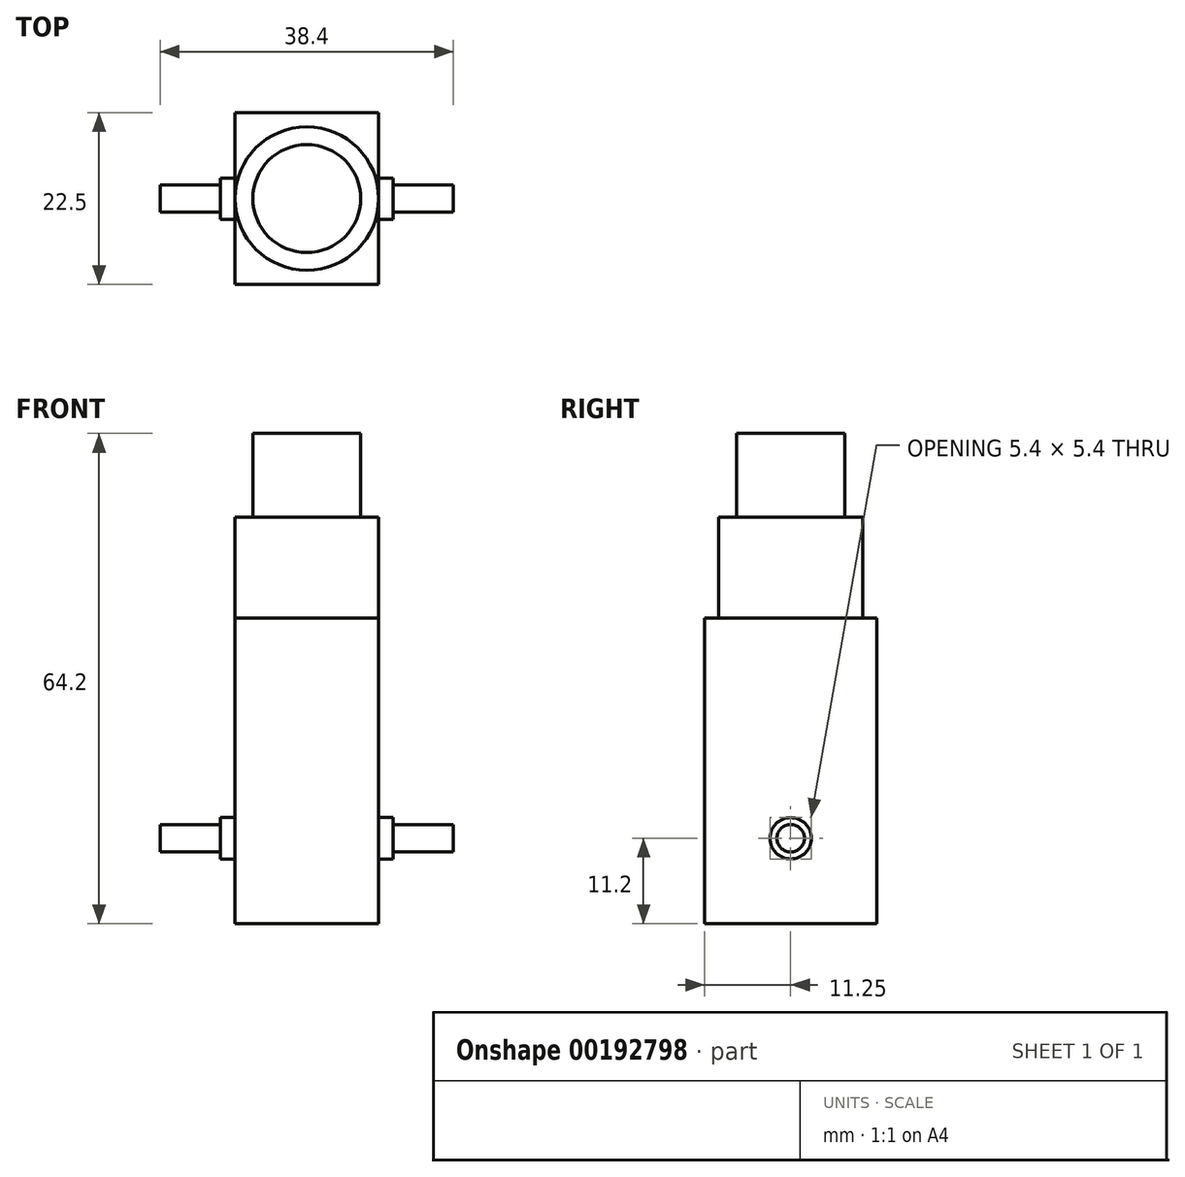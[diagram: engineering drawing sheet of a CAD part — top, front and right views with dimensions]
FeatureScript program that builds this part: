
annotation { "Feature Type Name" : "Feature", "Feature Type Description" : "" }
export const myFeature = defineFeature(function(context is Context, id is Id, definition is map)
    precondition{}
    {
        {
            var Q0;
            Q0=qCreatedBy(makeId("Top.planeOp"),FACE);
            var sketch = newSketch(context, id + "F0", { "sketchPlane" : qUnion([Q0])});
            skLineSegment(sketch, "E0.bottom", {"start": v(-9.4, 11.25) * mm, "end": v(9.4, 11.25) * mm});
            skLineSegment(sketch, "E0.top", {"start": v(-9.4, -11.25) * mm, "end": v(9.4, -11.25) * mm});
            skLineSegment(sketch, "E0.left", {"start": v(-9.4, 11.25) * mm, "end": v(-9.4, -11.25) * mm});
            skLineSegment(sketch, "E0.right", {"start": v(9.4, 11.25) * mm, "end": v(9.4, -11.25) * mm});
            skLineSegment(sketch, "E1", {"start": v(-9.4, 11.25) * mm, "end": v(9.4, -11.25) * mm, "construction": true});
            skSolve(sketch);
        }
        {
            var Q0;
            Q0=qSketchRegion(id+"F0",true);
            extrude(context, id + "F1", {"entities" : qUnion([Q0]), "depth" : 40 * mm});
        }
        {
            var Q0;
            Q0=qCreatedBy(makeId("Front.planeOp"),FACE);
            var sketch = newSketch(context, id + "F2", { "sketchPlane" : qUnion([Q0])});
            skLineSegment(sketch, "E2", {"start": v(0, 64.2) * mm, "end": v(0, 40) * mm});
            skLineSegment(sketch, "E3", {"start": v(0, 40) * mm, "end": v(9.4, 40) * mm});
            skLineSegment(sketch, "E4", {"start": v(9.4, 40) * mm, "end": v(9.4, 53.23) * mm});
            skLineSegment(sketch, "E5", {"start": v(9.4, 53.23) * mm, "end": v(7.06, 53.23) * mm});
            skLineSegment(sketch, "E6", {"start": v(7.06, 53.23) * mm, "end": v(7.06, 64.2) * mm});
            skLineSegment(sketch, "E7", {"start": v(7.06, 64.2) * mm, "end": v(0, 64.2) * mm});
            skSolve(sketch);
        }
        {
            var Q0;
            Q0=qSketchRegion(id+"F2",true);
            var Q1;
            Q1=sQuery(id+"F2.wireOp",EDGE,"E2");
            revolve(context, id + "F3", {"operationType" : NewBodyOperationType.ADD, "entities" : qUnion([Q0]), "axis" : qUnion([Q1]), "revolveType" : RevolveType.FULL});
        }
        {
            var Q0;
            Q0=qCreatedBy(makeId("Front.planeOp"),FACE);
            var sketch = newSketch(context, id + "F4", { "sketchPlane" : qUnion([Q0])});
            skLineSegment(sketch, "E8", {"start": v(9.4, 13.9) * mm, "end": v(11.3, 13.9) * mm});
            skLineSegment(sketch, "E9", {"start": v(11.3, 13.9) * mm, "end": v(11.3, 13) * mm});
            skLineSegment(sketch, "E10", {"start": v(11.3, 13) * mm, "end": v(19.2, 13) * mm});
            skLineSegment(sketch, "E11", {"start": v(19.2, 13) * mm, "end": v(19.2, 11.2) * mm});
            skLineSegment(sketch, "E12", {"start": v(19.2, 11.2) * mm, "end": v(9.4, 11.2) * mm});
            skLineSegment(sketch, "E13", {"start": v(9.4, 11.2) * mm, "end": v(9.4, 13.9) * mm});
            skLineSegment(sketch, "E14.MirrorCS", {"start": v(-9.4, 11.2) * mm, "end": v(-9.4, 13.9) * mm});
            skLineSegment(sketch, "E15.MirrorCS", {"start": v(-11.3, 13) * mm, "end": v(-19.2, 13) * mm});
            skLineSegment(sketch, "E16.MirrorCS", {"start": v(-19.2, 13) * mm, "end": v(-19.2, 11.2) * mm});
            skLineSegment(sketch, "E17.MirrorCS", {"start": v(-9.4, 13.9) * mm, "end": v(-11.3, 13.9) * mm});
            skLineSegment(sketch, "E18.MirrorCS", {"start": v(-19.2, 11.2) * mm, "end": v(-9.4, 11.2) * mm});
            skLineSegment(sketch, "E19.MirrorCS", {"start": v(-11.3, 13.9) * mm, "end": v(-11.3, 13) * mm});
            skLineSegment(sketch, "E20", {"start": v(-22.42, 11.2) * mm, "end": v(22.18, 11.2) * mm, "construction": true});
            skSolve(sketch);
        }
        {
            var Q0;
            Q0=qSketchRegion(id+"F4",true);
            var Q1;
            Q1=sQuery(id+"F4.wireOp",EDGE,"E20");
            revolve(context, id + "F5", {"operationType" : NewBodyOperationType.ADD, "entities" : qUnion([Q0]), "axis" : qUnion([Q1]), "revolveType" : RevolveType.FULL});
        }
    });
